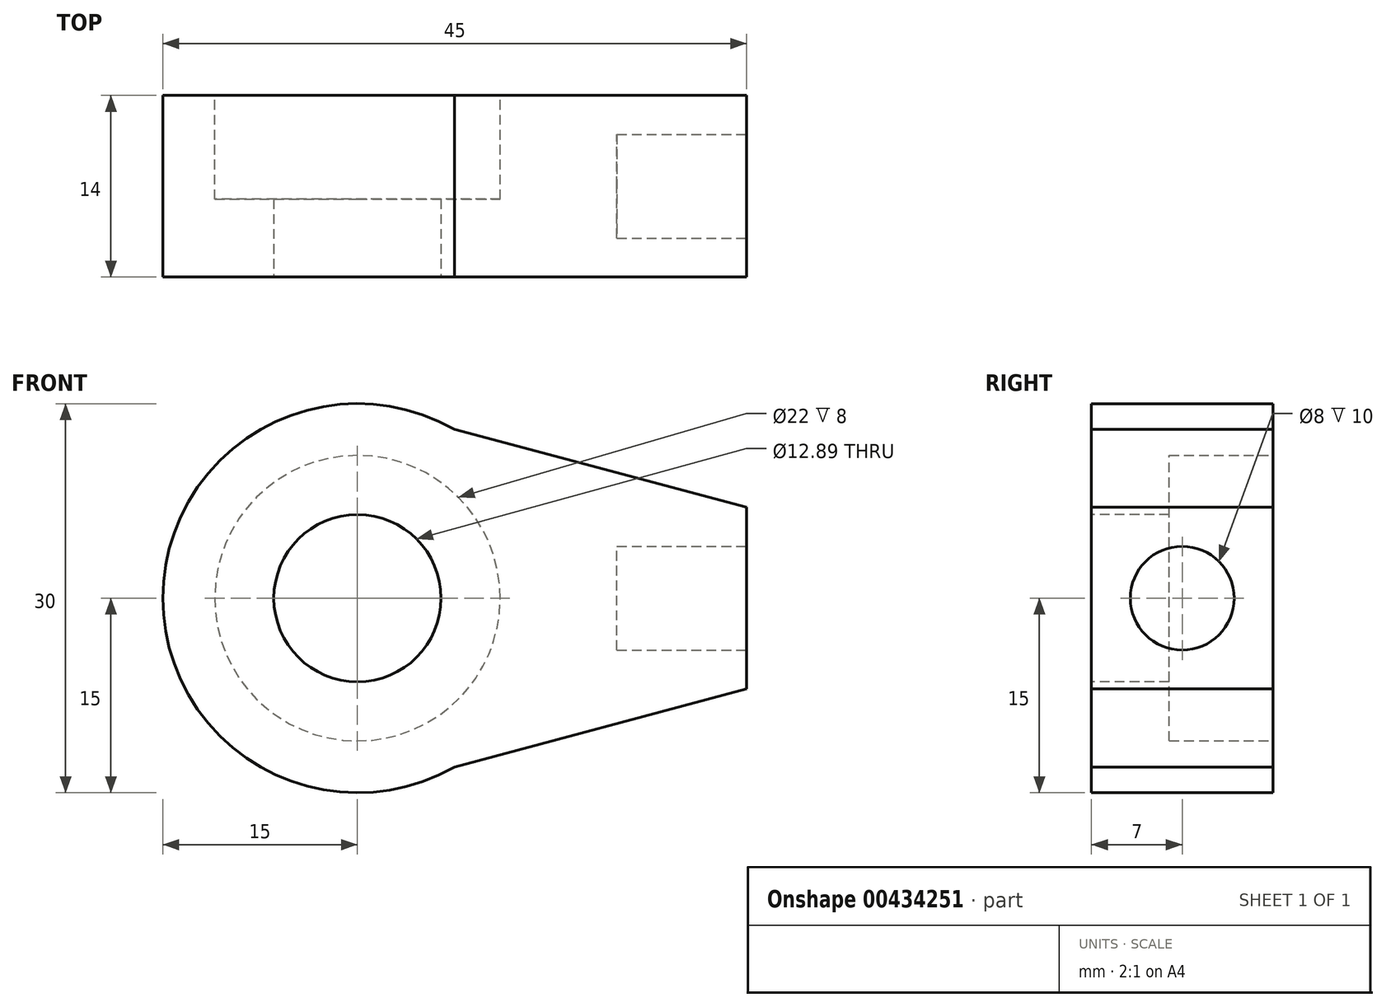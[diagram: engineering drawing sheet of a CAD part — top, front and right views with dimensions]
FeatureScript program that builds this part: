
annotation { "Feature Type Name" : "Feature", "Feature Type Description" : "" }
export const myFeature = defineFeature(function(context is Context, id is Id, definition is map)
    precondition{}
    {
        {
            var Q0;
            Q0=qCreatedBy(makeId("Front.planeOp"),FACE);
            var sketch = newSketch(context, id + "F0", { "sketchPlane" : qUnion([Q0])});
            skCircle(sketch, "E0", {"center": v(0, 0) * mm, "radius": 11 * mm});
            skCircle(sketch, "E1", {"center": v(0, 0) * mm, "radius": 15 * mm});
            skLineSegment(sketch, "E2", {"start": v(0, 0) * mm, "end": v(30, 0) * mm, "construction": true});
            skLineSegment(sketch, "E3", {"start": v(30, 0) * mm, "end": v(30, -7) * mm});
            skLineSegment(sketch, "E4.MirrorCS", {"start": v(30, 0) * mm, "end": v(30, 7) * mm});
            skLineSegment(sketch, "E5", {"start": v(0, -15) * mm, "end": v(30, -7) * mm});
            skLineSegment(sketch, "E6", {"start": v(0, 15) * mm, "end": v(30, 7) * mm});
            skSolve(sketch);
        }
        {
            var Q0;
            Q0 = qSketchRegion(id + "F0", true);
            extrude(context, id + "F1", {"entities" : qUnion([Q0]), "depth" : 14 * mm});
        }
        {
            var Q0;
            Q0=makeQuery(id+"F1.opExtrude","SWEPT_FACE",FACE,{"disambiguationData":[OSD([sQuery(id+"F0.wireOp",EDGE,"E3"),sQuery(id+"F0.wireOp",EDGE,"E4.MirrorCS")])]});
            var sketch = newSketch(context, id + "F2", { "sketchPlane" : qUnion([Q0])});
            skCircle(sketch, "E7", {"center": v(-7, 0) * mm, "radius": 4 * mm});
            skPoint(sketch, "E7.centerSnap0", {"position": v(-7, 7) * mm});
            skPoint(sketch, "E7.centerSnap1", {"position": v(0, 0) * mm});
            skSolve(sketch);
        }
        {
            var Q0;
            Q0 = qSketchRegion(id + "F2", true);
            extrude(context, id + "F3", {"entities" : qUnion([Q0]), "operationType" : NewBodyOperationType.REMOVE, "oppositeDirection" : true, "depth" : 10 * mm});
        }
        {
            var Q0;
            Q0=makeQuery(id+"F1.opExtrude","CAP_FACE",FACE,{"disambiguationData":[OSD([sQuery(id+"F0.wireOp",EDGE,"E0"),sQuery(id+"F0.wireOp",EDGE,"E1"),sQuery(id+"F0.wireOp",EDGE,"E3"),sQuery(id+"F0.wireOp",EDGE,"E4.MirrorCS"),sQuery(id+"F0.wireOp",EDGE,"E5"),sQuery(id+"F0.wireOp",EDGE,"E6")])],"isStart":false});
            var sketch = newSketch(context, id + "F4", { "sketchPlane" : qUnion([Q0])});
            skCircle(sketch, "E8", {"center": v(0, 0) * mm, "radius": 6.44 * mm});
            skCircle(sketch, "E9", {"center": v(0, 0) * mm, "radius": 11.27 * mm});
            skSolve(sketch);
        }
        {
            var Q0;
            Q0 = qSketchRegion(id + "F4", true);
            extrude(context, id + "F5", {"entities" : qUnion([Q0]), "operationType" : NewBodyOperationType.ADD, "oppositeDirection" : true, "depth" : 6 * mm});
        }
    });
